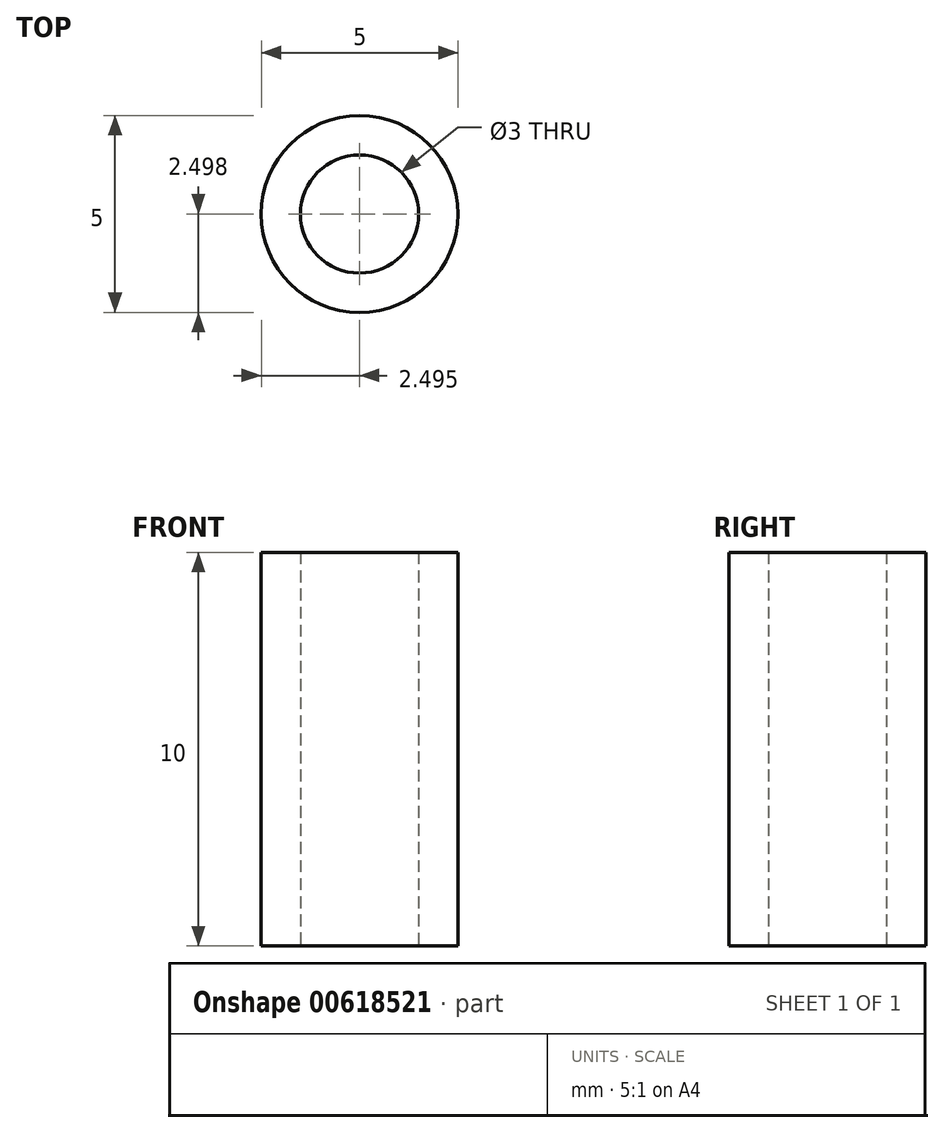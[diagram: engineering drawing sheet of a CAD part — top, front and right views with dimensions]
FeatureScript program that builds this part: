
annotation { "Feature Type Name" : "Feature", "Feature Type Description" : "" }
export const myFeature = defineFeature(function(context is Context, id is Id, definition is map)
    precondition{}
    {
        {
            var Q0;
            Q0=qCreatedBy(makeId("Top.planeOp"),FACE);
            var sketch = newSketch(context, id + "F0", { "sketchPlane" : qUnion([Q0])});
            skCircle(sketch, "E0", {"center": v(-39.18, 31.74) * mm, "radius": 2.5 * mm});
            skCircle(sketch, "E1", {"center": v(-39.18, 31.74) * mm, "radius": 1.5 * mm});
            skSolve(sketch);
        }
        {
            var Q0;
            Q0=qSketchRegion(id+"F0",true);
            extrude(context, id + "F1", {"entities" : qUnion([Q0]), "depth" : 10 * mm, "offsetDistance" : 25 * mm});
        }
    });
